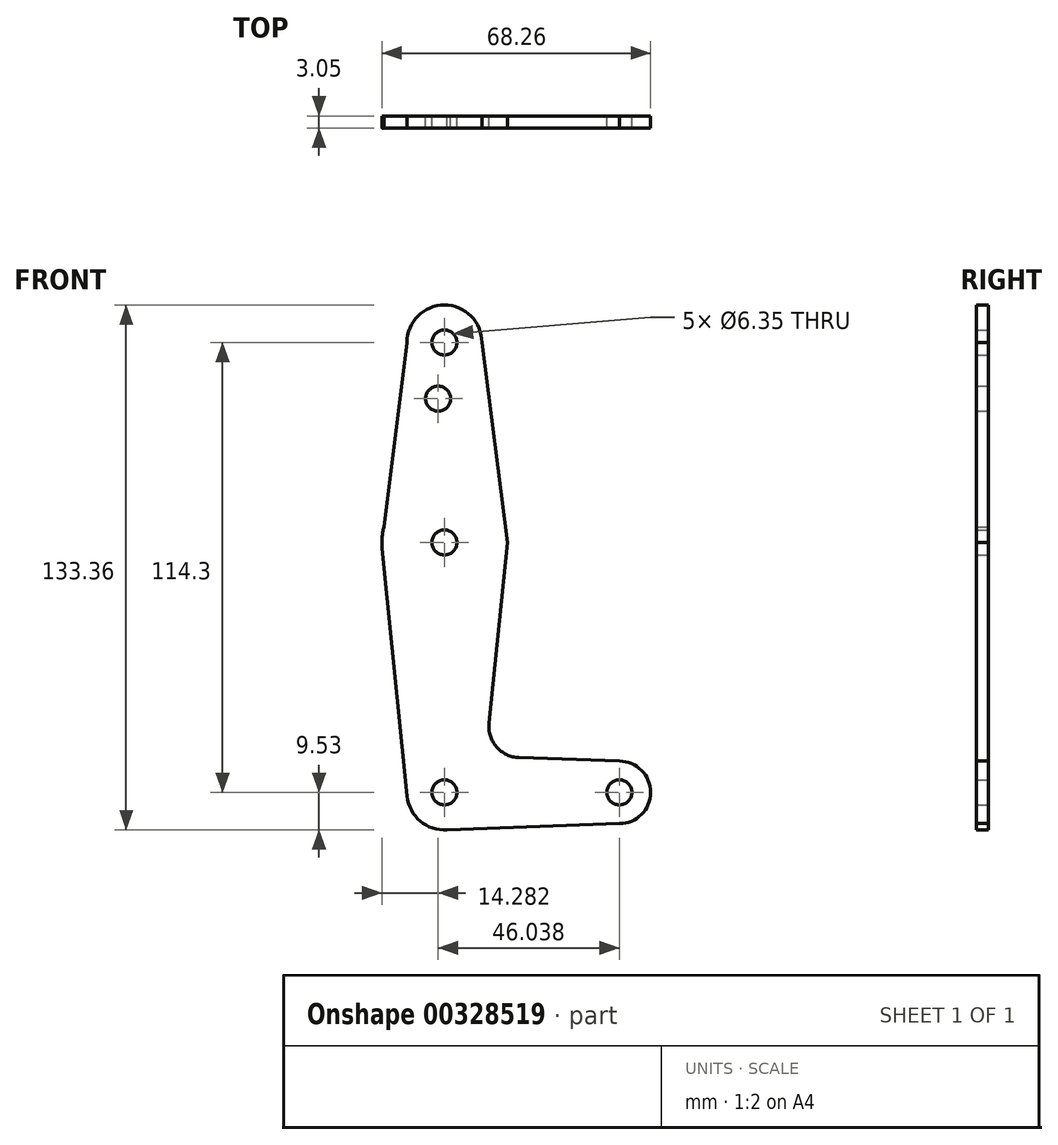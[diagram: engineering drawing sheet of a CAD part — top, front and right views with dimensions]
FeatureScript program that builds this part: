
annotation { "Feature Type Name" : "Feature", "Feature Type Description" : "" }
export const myFeature = defineFeature(function(context is Context, id is Id, definition is map)
    precondition{}
    {
        {
            var Q0;
            Q0=qCreatedBy(makeId("Front.planeOp"),FACE);
            var sketch = newSketch(context, id + "F0", { "sketchPlane" : qUnion([Q0])});
            skLineSegment(sketch, "E0", {"start": v(0, 114.3) * mm, "end": v(0, 0) * mm, "construction": true});
            skLineSegment(sketch, "E1", {"start": v(0, 0) * mm, "end": v(44.45, 0) * mm, "construction": true});
            skCircle(sketch, "E2", {"center": v(0, 114.3) * mm, "radius": 9.53 * mm});
            skCircle(sketch, "E3", {"center": v(0, 0) * mm, "radius": 9.53 * mm});
            skCircle(sketch, "E4", {"center": v(44.45, 0) * mm, "radius": 7.94 * mm});
            skCircle(sketch, "E5", {"center": v(0, 63.5) * mm, "radius": 15.88 * mm});
            skLineSegment(sketch, "E6", {"start": v(9.53, 114.3) * mm, "end": v(16, 63.5) * mm});
            skLineSegment(sketch, "E7", {"start": v(16, 63.5) * mm, "end": v(11.32, 17.6) * mm});
            skLineSegment(sketch, "E8", {"start": v(-9.53, 114.3) * mm, "end": v(-15.88, 63.5) * mm});
            skLineSegment(sketch, "E9", {"start": v(18.95, 8.85) * mm, "end": v(44.45, 7.94) * mm});
            skLineSegment(sketch, "E10", {"start": v(44.45, -7.94) * mm, "end": v(0, -9.53) * mm});
            skLineSegment(sketch, "E11", {"start": v(-15.8, 61.91) * mm, "end": v(-9.48, -0.95) * mm});
            skCircle(sketch, "E12", {"center": v(0, 114.3) * mm, "radius": 3.18 * mm});
            skCircle(sketch, "E13", {"center": v(-1.59, 100.03) * mm, "radius": 3.18 * mm});
            skCircle(sketch, "E14", {"center": v(0, 63.5) * mm, "radius": 3.18 * mm});
            skCircle(sketch, "E15", {"center": v(0, 0) * mm, "radius": 3.18 * mm});
            skCircle(sketch, "E16", {"center": v(44.45, 0) * mm, "radius": 3.18 * mm});
            skArc(sketch, "E17.filletArc", {"start": v(11.32, 17.6) * mm, "mid": v(13.24, 11.57) * mm, "end": v(18.95, 8.85) * mm});
            skSolve(sketch);
        }
        {
            var Q0;
            Q0 = qSketchRegion(id + "F0", true);
            extrude(context, id + "F1", {"entities" : qUnion([Q0]), "depth" : 3.05 * mm});
        }
    });
